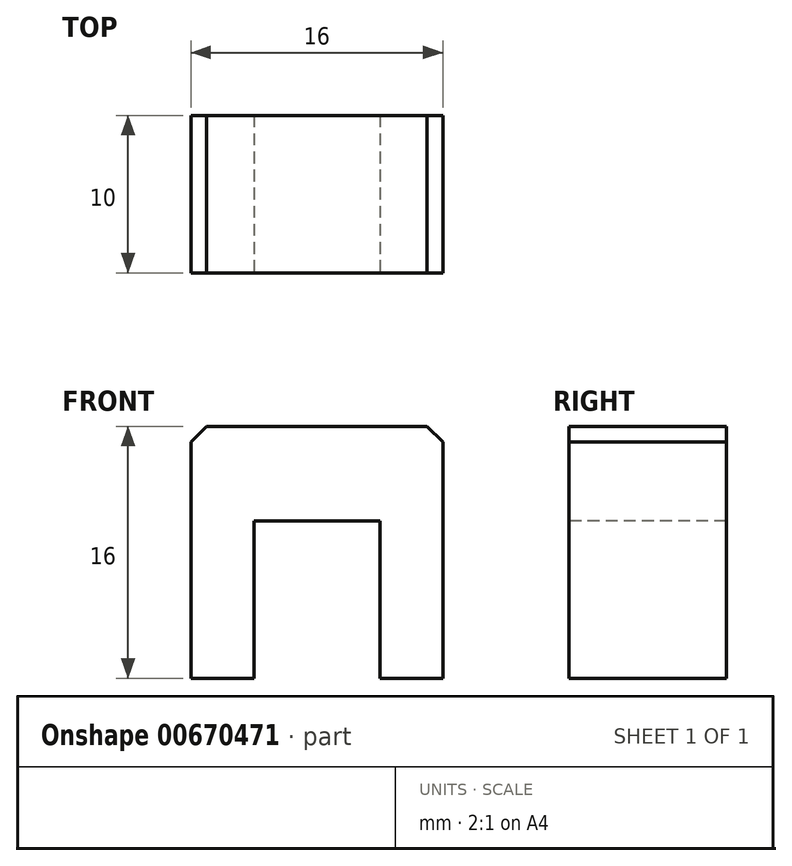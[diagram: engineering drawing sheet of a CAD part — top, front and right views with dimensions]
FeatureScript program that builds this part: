
annotation { "Feature Type Name" : "Feature", "Feature Type Description" : "" }
export const myFeature = defineFeature(function(context is Context, id is Id, definition is map)
    precondition{}
    {
        {
            var Q0;
            Q0=qCreatedBy(makeId("Front.planeOp"),FACE);
            var sketch = newSketch(context, id + "F0", { "sketchPlane" : qUnion([Q0])});
            skLineSegment(sketch, "E0.bottom", {"start": v(0, 16) * mm, "end": v(16, 16) * mm});
            skLineSegment(sketch, "E0.top", {"start": v(0, 0) * mm, "end": v(16, 0) * mm});
            skLineSegment(sketch, "E0.left", {"start": v(16, 16) * mm, "end": v(16, 0) * mm});
            skLineSegment(sketch, "E0.right", {"start": v(0, 16) * mm, "end": v(0, 0) * mm});
            skSolve(sketch);
        }
        {
            var Q0;
            Q0=makeQuery(id+"F0.imprint","IMPRINT",FACE,{"disambiguationData":[TD([[makeQuery(id+"F0.imprint","IMPRINT",EDGE,{"derivedFrom":sQuery(id+"F0.wireOp",EDGE,"E0.bottom")}),-1.0]])]});
            extrude(context, id + "F1", {"entities" : qUnion([Q0]), "depth" : 10 * mm, "offsetDistance" : 25 * mm});
        }
        {
            var Q0;
            Q0=makeQuery(id+"F1.opExtrude","CAP_FACE",FACE,{"disambiguationData":[OSD([sQuery(id+"F0.wireOp",EDGE,"E0.bottom"),sQuery(id+"F0.wireOp",EDGE,"E0.top"),sQuery(id+"F0.wireOp",EDGE,"E0.left"),sQuery(id+"F0.wireOp",EDGE,"E0.right")])],"isStart":false});
            var sketch = newSketch(context, id + "F2", { "sketchPlane" : qUnion([Q0])});
            skLineSegment(sketch, "E1.bottom", {"start": v(4, 10) * mm, "end": v(12, 10) * mm});
            skLineSegment(sketch, "E1.top", {"start": v(4, 0) * mm, "end": v(12, 0) * mm});
            skLineSegment(sketch, "E1.left", {"start": v(4, 10) * mm, "end": v(4, 0) * mm});
            skLineSegment(sketch, "E1.right", {"start": v(12, 10) * mm, "end": v(12, 0) * mm});
            skPoint(sketch, "E2", {"position": v(8, 16) * mm});
            skPoint(sketch, "E3", {"position": v(8, 10) * mm});
            skLineSegment(sketch, "E4", {"start": v(8, 16) * mm, "end": v(8, 10) * mm, "construction": true});
            skSolve(sketch);
        }
        {
            var Q0;
            Q0=makeQuery(id+"F2.imprint","IMPRINT",FACE,{"disambiguationData":[TD([[makeQuery(id+"F2.imprint","IMPRINT",EDGE,{"derivedFrom":sQuery(id+"F2.wireOp",EDGE,"E1.bottom")}),-1.0]])]});
            extrude(context, id + "F3", {"entities" : qUnion([Q0]), "operationType" : NewBodyOperationType.REMOVE, "endBound" : BoundingType.THROUGH_ALL, "oppositeDirection" : true, "depth" : 5 * mm, "offsetDistance" : 25 * mm});
        }
        {
            var Q0;
            Q0=makeQuery(id+"F1.opExtrude","SWEPT_EDGE",EDGE,{"disambiguationData":[OSD([sQuery(id+"F0.wireOp",EDGE,"E0.bottom"),sQuery(id+"F0.wireOp",EDGE,"E0.right")])]});
            var Q1;
            Q1=makeQuery(id+"F1.opExtrude","SWEPT_EDGE",EDGE,{"disambiguationData":[OSD([sQuery(id+"F0.wireOp",EDGE,"E0.bottom"),sQuery(id+"F0.wireOp",EDGE,"E0.left")])]});
            chamfer(context, id + "F4", {"entities" : qUnion([Q0, Q1]), "width" : 1 * mm, "tangentPropagation" : true});
        }
    });
